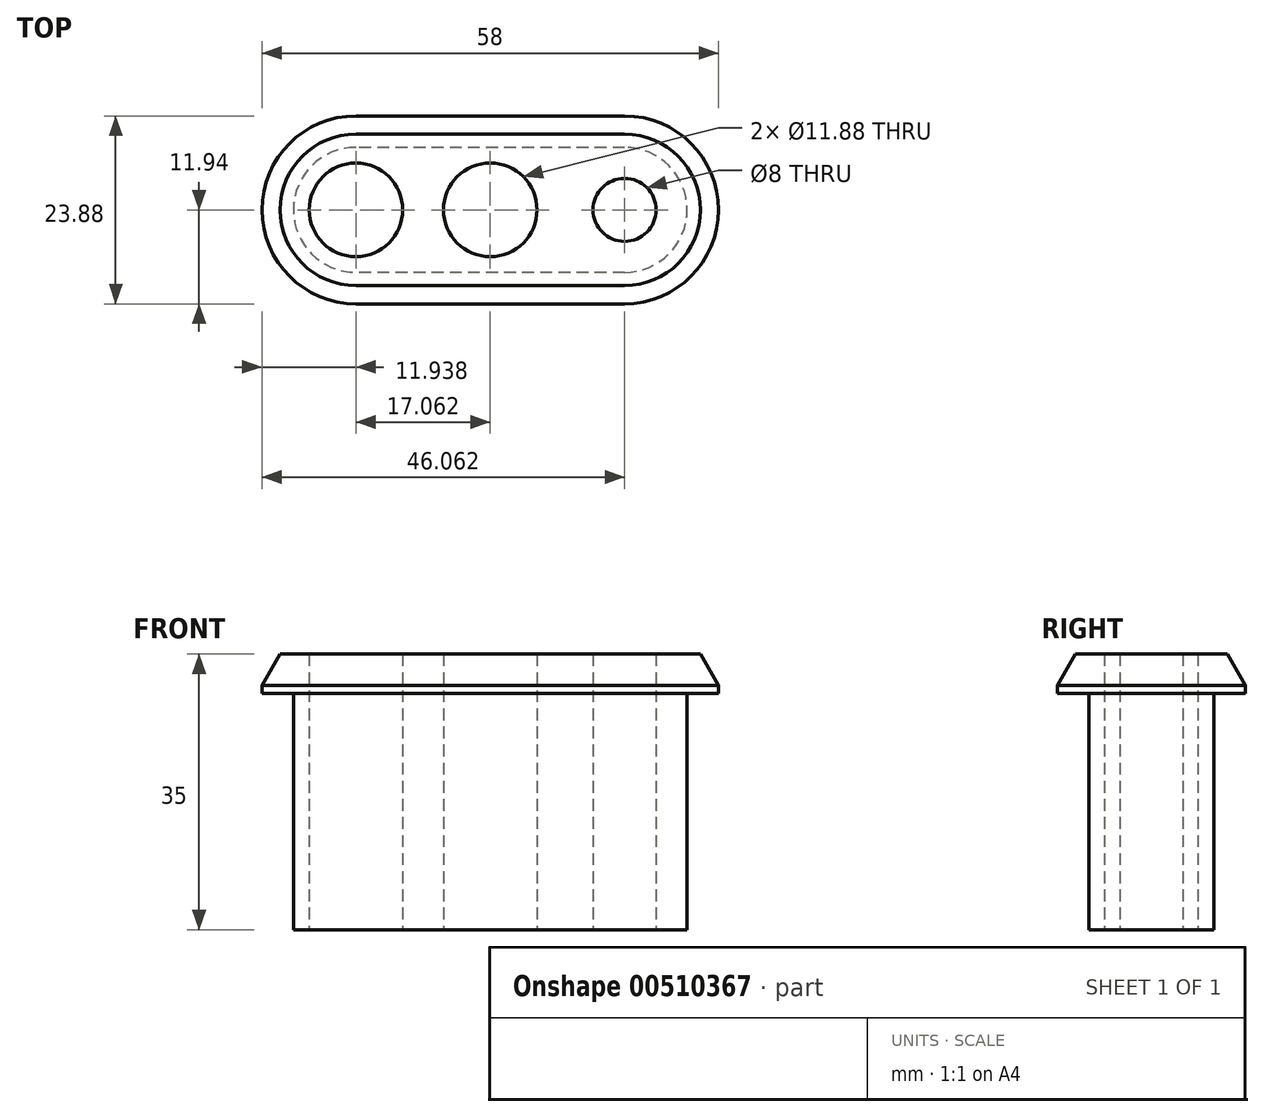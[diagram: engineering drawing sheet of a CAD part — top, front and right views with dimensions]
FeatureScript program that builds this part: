
annotation { "Feature Type Name" : "Feature", "Feature Type Description" : "" }
export const myFeature = defineFeature(function(context is Context, id is Id, definition is map)
    precondition{}
    {
        {
            var Q0;
            Q0=qCreatedBy(makeId("Top.planeOp"),FACE);
            var sketch = newSketch(context, id + "F0", { "sketchPlane" : qUnion([Q0])});
            skLineSegment(sketch, "E0.bottom", {"start": v(0, -7.94) * mm, "end": v(-17.06, -7.94) * mm});
            skLineSegment(sketch, "E0.top", {"start": v(0, 7.94) * mm, "end": v(-17.06, 7.94) * mm});
            skPoint(sketch, "E0.middle", {"position": v(0, 0) * mm});
            skArc(sketch, "E1", {"start": v(-17.06, 7.94) * mm, "mid": v(-25, 0) * mm, "end": v(-17.06, -7.94) * mm});
            skPoint(sketch, "E2.center.orphan", {"position": v(-25, 0) * mm});
            skPoint(sketch, "E3.MirrorP", {"position": v(25, 0) * mm});
            skLineSegment(sketch, "E4.MirrorCS", {"start": v(0, 7.94) * mm, "end": v(17.06, 7.94) * mm});
            skLineSegment(sketch, "E5.MirrorCS", {"start": v(0, -7.94) * mm, "end": v(17.06, -7.94) * mm});
            skArc(sketch, "E6.MirrorC", {"start": v(17.06, 7.94) * mm, "mid": v(25, 0) * mm, "end": v(17.06, -7.94) * mm});
            skCircle(sketch, "E7", {"center": v(-17.06, 0) * mm, "radius": 5.94 * mm});
            skCircle(sketch, "E8", {"center": v(0, 0) * mm, "radius": 5.94 * mm});
            skCircle(sketch, "E9", {"center": v(17.06, 0) * mm, "radius": 4 * mm});
            skSolve(sketch);
        }
        {
            var Q0;
            Q0=makeQuery(id+"F0.imprint","IMPRINT",FACE,{"disambiguationData":[TD([[makeQuery(id+"F0.imprint","IMPRINT",EDGE,{"derivedFrom":sQuery(id+"F0.wireOp",EDGE,"E0.bottom")}),-1.0]])]});
            extrude(context, id + "F1", {"entities" : qUnion([Q0]), "depth" : 30 * mm});
        }
        {
            var Q0;
            Q0=makeQuery(id+"F1.opExtrude","CAP_FACE",FACE,{"disambiguationData":[OSD([sQuery(id+"F0.wireOp",EDGE,"E0.bottom"),sQuery(id+"F0.wireOp",EDGE,"E0.top"),sQuery(id+"F0.wireOp",EDGE,"E1"),sQuery(id+"F0.wireOp",EDGE,"E4.MirrorCS"),sQuery(id+"F0.wireOp",EDGE,"E5.MirrorCS"),sQuery(id+"F0.wireOp",EDGE,"E6.MirrorC"),sQuery(id+"F0.wireOp",EDGE,"E7"),sQuery(id+"F0.wireOp",EDGE,"E8"),sQuery(id+"F0.wireOp",EDGE,"E9")])],"isStart":false});
            var sketch = newSketch(context, id + "F2", { "sketchPlane" : qUnion([Q0])});
            skLineSegment(sketch, "E10.0", {"start": v(-17.06, 7.94) * mm, "end": v(17.06, 7.94) * mm});
            skArc(sketch, "E10.1", {"start": v(-17.06, 7.94) * mm, "mid": v(-25, 0) * mm, "end": v(-17.06, -7.94) * mm});
            skArc(sketch, "E10.2", {"start": v(17.06, 7.94) * mm, "mid": v(25, 0) * mm, "end": v(17.06, -7.94) * mm});
            skLineSegment(sketch, "E10.3", {"start": v(17.06, -7.94) * mm, "end": v(-17.06, -7.94) * mm});
            skArc(sketch, "E11.0", {"start": v(17.06, 11.94) * mm, "mid": v(29, 0) * mm, "end": v(17.06, -11.94) * mm});
            skLineSegment(sketch, "E11.1", {"start": v(-17.06, 11.94) * mm, "end": v(17.06, 11.94) * mm});
            skArc(sketch, "E11.2", {"start": v(-17.06, 11.94) * mm, "mid": v(-29, 0) * mm, "end": v(-17.06, -11.94) * mm});
            skLineSegment(sketch, "E11.3", {"start": v(17.06, -11.94) * mm, "end": v(-17.06, -11.94) * mm});
            skSolve(sketch);
        }
        {
            var Q0;
            Q0=makeQuery(id+"F2.imprint","IMPRINT",FACE,{"disambiguationData":[TD([[makeQuery(id+"F2.imprint","IMPRINT",EDGE,{"derivedFrom":sQuery(id+"F2.wireOp",EDGE,"E10.0")}),1.0]])]});
            var Q1;
            Q1=makeQuery(id+"F2.imprint","IMPRINT",FACE,{"disambiguationData":[TD([[makeQuery(id+"F2.imprint","IMPRINT",EDGE,{"derivedFrom":sQuery(id+"F2.wireOp",EDGE,"E10.0")}),-1.0]])]});
            extrude(context, id + "F3", {"entities" : qUnion([Q0, Q1]), "operationType" : NewBodyOperationType.ADD, "depth" : 5 * mm});
        }
        {
            var Q0;
            Q0=makeQuery(id+"F3.opExtrude","CAP_EDGE",EDGE,{"disambiguationData":[OSD([sQuery(id+"F2.wireOp",EDGE,"E11.3")])],"isStart":false});
            var Q1;
            Q1=makeQuery(id+"F3.opExtrude","CAP_EDGE",EDGE,{"disambiguationData":[OSD([sQuery(id+"F2.wireOp",EDGE,"E11.2")])],"isStart":false});
            var Q2;
            Q2=makeQuery(id+"F3.opExtrude","CAP_EDGE",EDGE,{"disambiguationData":[OSD([sQuery(id+"F2.wireOp",EDGE,"E11.1")])],"isStart":false});
            var Q3;
            Q3=makeQuery(id+"F3.opExtrude","CAP_EDGE",EDGE,{"disambiguationData":[OSD([sQuery(id+"F2.wireOp",EDGE,"E11.0")])],"isStart":false});
            chamfer(context, id + "F4", {"entities" : qUnion([Q0, Q1, Q2, Q3]), "chamferType" : ChamferType.OFFSET_ANGLE, "width" : 4 * mm, "oppositeDirection" : false, "angle" : 30 * degree, "tangentPropagation" : true});
        }
    });
